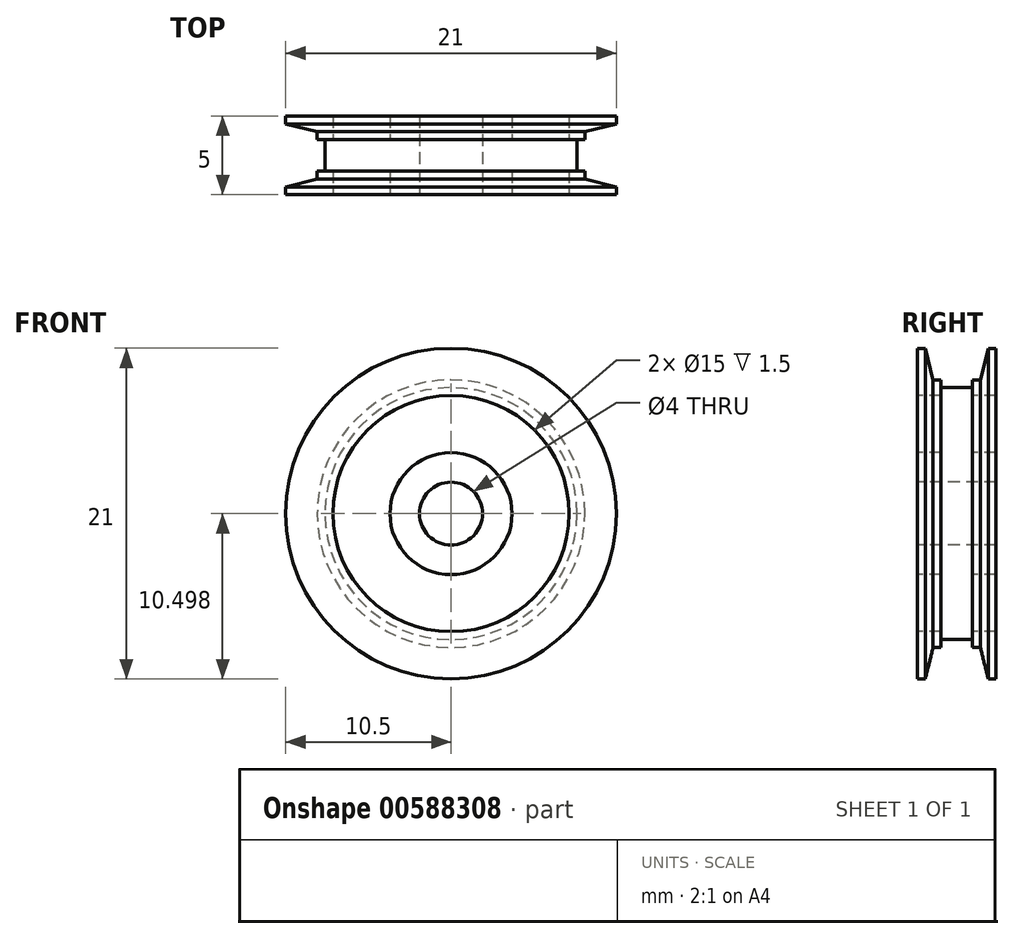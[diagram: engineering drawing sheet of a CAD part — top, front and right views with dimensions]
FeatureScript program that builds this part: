
annotation { "Feature Type Name" : "Feature", "Feature Type Description" : "" }
export const myFeature = defineFeature(function(context is Context, id is Id, definition is map)
    precondition{}
    {
        {
            var Q0;
            Q0=qCreatedBy(makeId("Right.planeOp"),FACE);
            var sketch = newSketch(context, id + "F0", { "sketchPlane" : qUnion([Q0])});
            skLineSegment(sketch, "E0", {"start": v(-95.37, 9.25) * mm, "end": v(-41.61, 9.25) * mm, "construction": true});
            skLineSegment(sketch, "E1", {"start": v(-26, 63) * mm, "end": v(-26, 16.75) * mm, "construction": true});
            skPoint(sketch, "E2.orphan", {"position": v(-26, 16.75) * mm});
            skLineSegment(sketch, "E3", {"start": v(-23.5, 19.75) * mm, "end": v(-23.5, 16.75) * mm});
            skLineSegment(sketch, "E4", {"start": v(-23.5, 19.75) * mm, "end": v(-24, 19.75) * mm});
            skPoint(sketch, "E5.endSnap0", {"position": v(-25, 17.75) * mm});
            skLineSegment(sketch, "E6", {"start": v(-25, 17.75) * mm, "end": v(-25, 17.25) * mm});
            skLineSegment(sketch, "E7", {"start": v(-24, 19.75) * mm, "end": v(-24.5, 17.75) * mm});
            skLineSegment(sketch, "E8.trimOffspring", {"start": v(-24, 19.75) * mm, "end": v(-23.5, 19.75) * mm});
            skLineSegment(sketch, "E9.MirrorCS", {"start": v(-28.5, 19.75) * mm, "end": v(-28.5, 16.75) * mm});
            skLineSegment(sketch, "E10.MirrorCS", {"start": v(-28, 19.75) * mm, "end": v(-28.5, 19.75) * mm});
            skLineSegment(sketch, "E11.MirrorCS", {"start": v(-28, 19.75) * mm, "end": v(-27.5, 17.75) * mm});
            skLineSegment(sketch, "E12.MirrorCS", {"start": v(-27, 17.75) * mm, "end": v(-27, 17.25) * mm});
            skLineSegment(sketch, "E13", {"start": v(-27.5, 17.75) * mm, "end": v(-27, 17.75) * mm});
            skLineSegment(sketch, "E14", {"start": v(-25, 17.75) * mm, "end": v(-24.5, 17.75) * mm});
            skLineSegment(sketch, "E15.trimOffspring", {"start": v(-26, 11.25) * mm, "end": v(-26, -43.93) * mm, "construction": true});
            skPoint(sketch, "E16.orphan", {"position": v(-25, 16.75) * mm});
            skPoint(sketch, "E17.orphan", {"position": v(-26, 19.75) * mm});
            skLineSegment(sketch, "E18.trimOffspring", {"start": v(-26, 9.25) * mm, "end": v(-97.5, 9.25) * mm, "construction": true});
            skLineSegment(sketch, "E19", {"start": v(-41.61, 9.25) * mm, "end": v(-26, 9.25) * mm});
            skLineSegment(sketch, "E20", {"start": v(-26, 9.25) * mm, "end": v(-41, 9.25) * mm});
            skLineSegment(sketch, "E21", {"start": v(-26, 9.25) * mm, "end": v(-11, 9.25) * mm});
            skPoint(sketch, "E22.orphan", {"position": v(-28.5, 9.25) * mm});
            skPoint(sketch, "E23.orphan", {"position": v(-23.5, 9.25) * mm});
            skLineSegment(sketch, "E24", {"start": v(-23.5, 16.75) * mm, "end": v(-25, 16.75) * mm});
            skLineSegment(sketch, "E25", {"start": v(-28.5, 11.25) * mm, "end": v(-23.5, 11.25) * mm});
            skLineSegment(sketch, "E26", {"start": v(-26, 9.25) * mm, "end": v(-26, 11.25) * mm});
            skLineSegment(sketch, "E27", {"start": v(-25, 13.12) * mm, "end": v(-23.5, 13.12) * mm});
            skPoint(sketch, "E28.end.orphan", {"position": v(-23.5, 13) * mm});
            skLineSegment(sketch, "E29", {"start": v(-27, 13.12) * mm, "end": v(-28.5, 13.12) * mm});
            skLineSegment(sketch, "E30", {"start": v(-25, 16.75) * mm, "end": v(-25, 13.12) * mm});
            skLineSegment(sketch, "E31", {"start": v(-27, 16.75) * mm, "end": v(-27, 13.12) * mm});
            skLineSegment(sketch, "E32", {"start": v(-27, 16.75) * mm, "end": v(-28.5, 16.75) * mm});
            skLineSegment(sketch, "E33", {"start": v(-27, 17.25) * mm, "end": v(-25, 17.25) * mm});
            skLineSegment(sketch, "E34.trimOffspring", {"start": v(-28.5, 13.12) * mm, "end": v(-28.5, 11.25) * mm});
            skLineSegment(sketch, "E35.trimOffspring", {"start": v(-23.5, 13.12) * mm, "end": v(-23.5, 11.25) * mm});
            skPoint(sketch, "E36.trimOffspring.end.orphan", {"position": v(-22.9, 11.25) * mm});
            skPoint(sketch, "E37.start.orphan", {"position": v(-29.11, 11.25) * mm});
            skPoint(sketch, "E38.end.orphan", {"position": v(-41, 11.25) * mm});
            skSolve(sketch);
        }
        {
            var Q0;
            Q0=makeQuery(id+"F0.imprint","IMPRINT",FACE,{"disambiguationData":[TD([[makeQuery(id+"F0.imprint","IMPRINT",EDGE,{"derivedFrom":sQuery(id+"F0.wireOp",EDGE,"E7")}),1.0]])]});
            var Q1;
            {var subQ0=sQuery(id+"F0.wireOp",EDGE,"z3ZhSZwS-oDT9-VPiS-UUG8-cDI0FaQCiPbm");Q1=makeQuery(id+"F0.imprint","IMPRINT",FACE,{"disambiguationData":[TD([[makeQuery(id+"F0.imprint","IMPRINT",EDGE,{"derivedFrom":subQ0}),-1.0]])]});}
            var Q2;
            Q2=makeQuery(id+"F0.imprint","IMPRINT",FACE,{"disambiguationData":[TD([[makeQuery(id+"F0.imprint","IMPRINT",EDGE,{"derivedFrom":sQuery(id+"F0.wireOp",EDGE,"E9.MirrorCS")}),1.0]])]});
            var Q3;
            Q3=makeQuery(id+"F0.imprint","IMPRINT",FACE,{"disambiguationData":[TD([[makeQuery(id+"F0.imprint","IMPRINT",EDGE,{"derivedFrom":sQuery(id+"F0.wireOp",EDGE,"z3ZhSZwS-oDT9-VPiS-UUG8-cDI0FaQCiPbm")}),1.0]])]});
            var Q4;
            {var subQ0=sQuery(id+"F0.wireOp",EDGE,"E34.trimOffspring");Q4=makeQuery(id+"F0.imprint","IMPRINT",FACE,{"disambiguationData":[TD([[makeQuery(id+"F0.imprint","IMPRINT",EDGE,{"derivedFrom":subQ0}),1.0]])]});}
            var Q5;
            {var subQ0=sQuery(id+"F0.wireOp",EDGE,"E35.trimOffspring");Q5=makeQuery(id+"F0.imprint","IMPRINT",FACE,{"disambiguationData":[TD([[makeQuery(id+"F0.imprint","IMPRINT",EDGE,{"derivedFrom":subQ0}),-1.0]])]});}
            var Q6;
            Q6=sQuery(id+"F0.wireOp",EDGE,"E19");
            revolve(context, id + "F1", {"surfaceOperationType" : NewSurfaceOperationType.NEW, "entities" : qUnion([Q0, Q1, Q2, Q3, Q4, Q5]), "axis" : qUnion([Q6]), "revolveType" : RevolveType.FULL});
        }
    });
